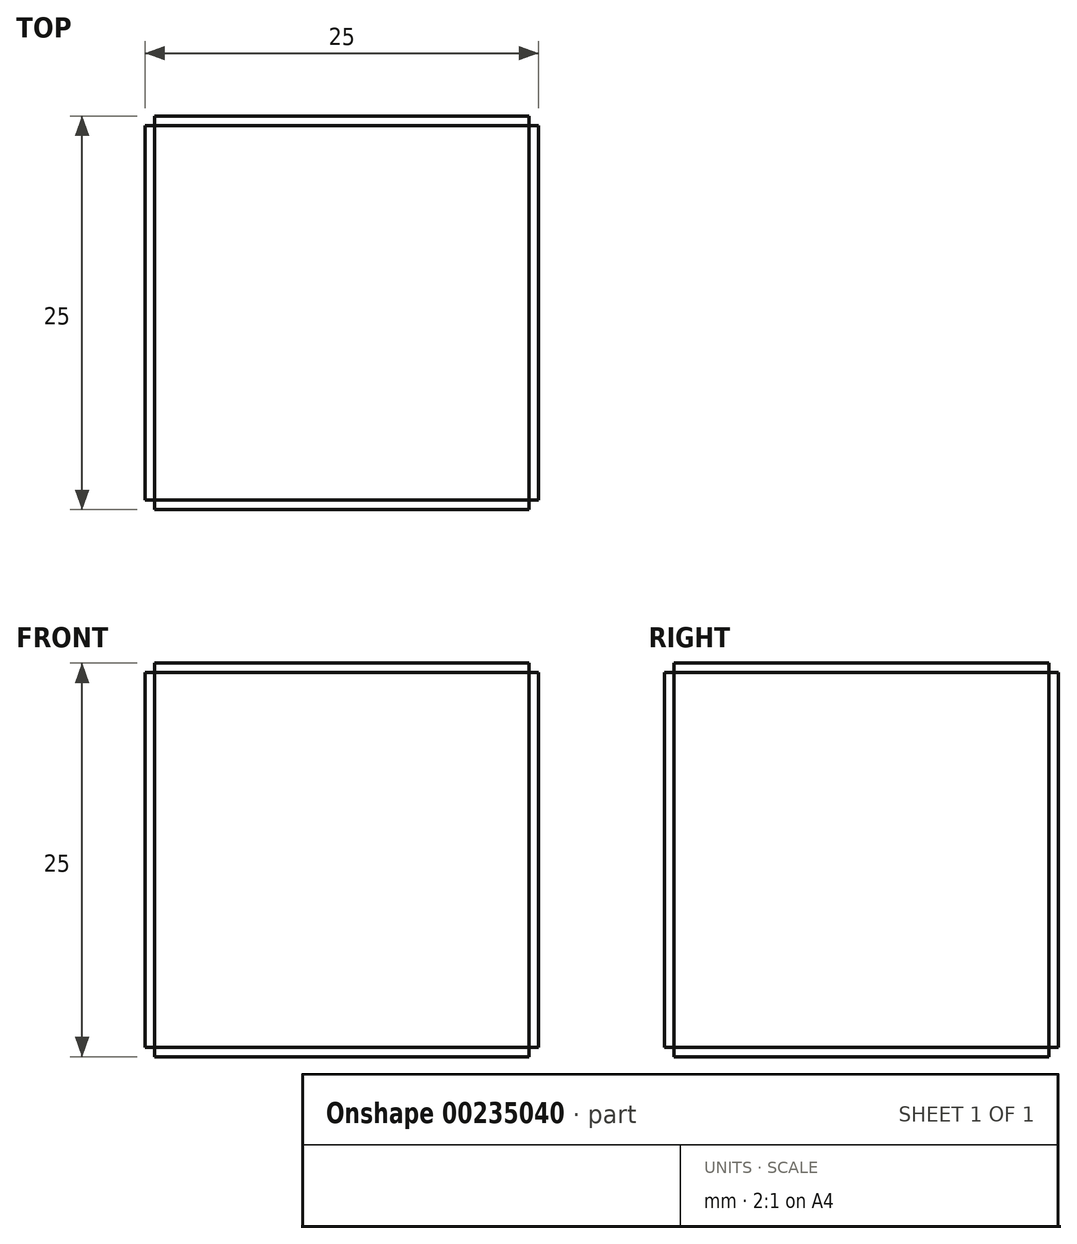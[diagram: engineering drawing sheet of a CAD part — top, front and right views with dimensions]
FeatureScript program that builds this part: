
annotation { "Feature Type Name" : "Feature", "Feature Type Description" : "" }
export const myFeature = defineFeature(function(context is Context, id is Id, definition is map)
    precondition{}
    {
        {
            var Q0;
            Q0=qCreatedBy(makeId("Front.planeOp"),FACE);
            var sketch = newSketch(context, id + "F0", { "sketchPlane" : qUnion([Q0])});
            skLineSegment(sketch, "E0.bottom", {"start": v(-11.9, 11.9) * mm, "end": v(11.9, 11.9) * mm});
            skLineSegment(sketch, "E0.top", {"start": v(-11.9, -11.9) * mm, "end": v(11.9, -11.9) * mm});
            skLineSegment(sketch, "E0.left", {"start": v(-11.9, 11.9) * mm, "end": v(-11.9, -11.9) * mm});
            skLineSegment(sketch, "E0.right", {"start": v(11.9, 11.9) * mm, "end": v(11.9, -11.9) * mm});
            skSolve(sketch);
        }
        {
            var Q0;
            Q0=qCreatedBy(makeId("Right.planeOp"),FACE);
            var sketch = newSketch(context, id + "F1", { "sketchPlane" : qUnion([Q0])});
            skLineSegment(sketch, "E1.bottom", {"start": v(-11.9, 11.9) * mm, "end": v(11.9, 11.9) * mm});
            skLineSegment(sketch, "E1.top", {"start": v(-11.9, -11.9) * mm, "end": v(11.9, -11.9) * mm});
            skLineSegment(sketch, "E1.left", {"start": v(-11.9, 11.9) * mm, "end": v(-11.9, -11.9) * mm});
            skLineSegment(sketch, "E1.right", {"start": v(11.9, 11.9) * mm, "end": v(11.9, -11.9) * mm});
            skSolve(sketch);
        }
        {
            var Q0;
            Q0=qCreatedBy(makeId("Top.planeOp"),FACE);
            var sketch = newSketch(context, id + "F2", { "sketchPlane" : qUnion([Q0])});
            skLineSegment(sketch, "E2.bottom", {"start": v(-11.9, 11.9) * mm, "end": v(11.9, 11.9) * mm});
            skLineSegment(sketch, "E2.top", {"start": v(-11.9, -11.9) * mm, "end": v(11.9, -11.9) * mm});
            skLineSegment(sketch, "E2.left", {"start": v(-11.9, 11.9) * mm, "end": v(-11.9, -11.9) * mm});
            skLineSegment(sketch, "E2.right", {"start": v(11.9, 11.9) * mm, "end": v(11.9, -11.9) * mm});
            skSolve(sketch);
        }
        {
            var Q0;
            Q0 = qSketchRegion(id + "F0", true);
            extrude(context, id + "F3", {"entities" : qUnion([Q0]), "depth" : 12.5 * mm, "hasSecondDirection" : true, "secondDirectionOppositeDirection" : true, "secondDirectionDepth" : 12.5 * mm});
        }
        {
            var Q0;
            Q0 = qSketchRegion(id + "F1", true);
            extrude(context, id + "F4", {"entities" : qUnion([Q0]), "operationType" : NewBodyOperationType.ADD, "depth" : 12.5 * mm, "hasSecondDirection" : true, "secondDirectionOppositeDirection" : true, "secondDirectionDepth" : 12.5 * mm});
        }
        {
            var Q0;
            Q0 = qSketchRegion(id + "F2", true);
            extrude(context, id + "F5", {"entities" : qUnion([Q0]), "operationType" : NewBodyOperationType.ADD, "depth" : 12.5 * mm, "hasSecondDirection" : true, "secondDirectionOppositeDirection" : true, "secondDirectionDepth" : 12.5 * mm});
        }
    });
